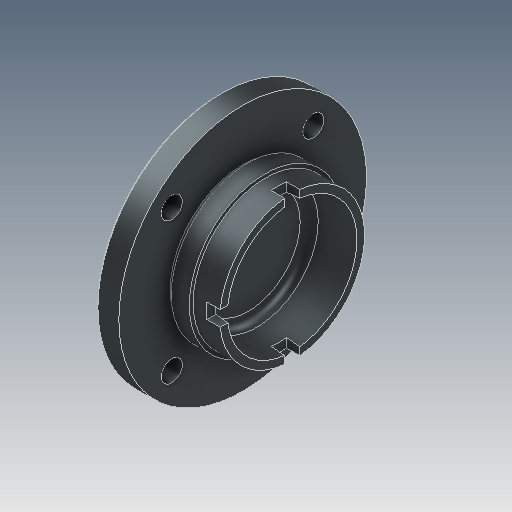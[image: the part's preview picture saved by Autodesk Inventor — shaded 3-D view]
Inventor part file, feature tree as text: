
AUTODESK INVENTOR PART (.ipt)
format: ipt  version: 2025 (Build 290162000, 162)  size: 222,208 bytes
history: native  units: in
note: dims shown in document units (in); Inventor stores cm internally (conversion verified against a paired STEP export)
features: sketch x5, extrude x3, revolve x1, chamfer x1, fillet x1
ambient origin geometry x8: Origin, YZ Plane, XZ Plane, XY Plane, X Axis, Y Axis, Z Axis, Center Point
bodies: 实体1 (feature_tree)
feature tree (11):
  revolve  "旋转1"  [1 undecoded]
  extrude  "拉伸1"  Depth=0.4724in
  extrude  "拉伸2"  Depth=1.4961in
  extrude  "拉伸3"  Depth=0.0984in
  chamfer  "倒角1"  Angle=45.0deg  [1 undecoded]
  fillet  "圆角1"  Radius=0.0394in
  sketch  "草图1"  dims[d3=0.3937in d0=0.4331in d1=1.811in d2=2.5591in]
  sketch  "草图2"  dims[d6=1.5748in d7=1.4961in]
  sketch  "草图3"  dims[d8=0.4724in d9=0.0984in]
  sketch  "草图4"  dims[d10=1.4961in d11=45.0deg d12=0.0394in d13=0.5906in d14=1.3386in d15=0.5792in d16=90.0deg d17=0.2756in d18=0.315in d19=0.0in d20=0.2756in d21=0.315in d22=0.0in d23=0.4331in d24=2.0669in d25=1.5748in d27=360.0deg d29=0.315in d30=0.0in d31=0.0394in d32=0.0787in d33=45.0deg d34=0.1969in d35=45.0deg]
  sketch  "草图 - 环形阵列1"  dims[d4=1.0236in d5=0.4724in]
note: 2 required parameter values undecoded (feature->parameter linkage not recoverable at this tier; creation-order binding heuristic only, values carry confidence <= 0.55)